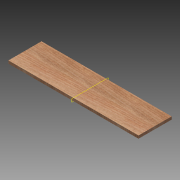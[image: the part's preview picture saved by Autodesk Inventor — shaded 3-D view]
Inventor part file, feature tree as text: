
AUTODESK INVENTOR PART (.ipt)
format: ipt  version: 2015 (Build 190159000, 159)  size: 84,992 bytes
history: native  units: in
note: dims shown in document units (in); Inventor stores cm internally (conversion verified against a paired STEP export)
features: extrude x1, plane x1, sketch x1
ambient origin geometry x8: Origin, YZ Plane, XZ Plane, XY Plane, X Axis, Y Axis, Z Axis, Center Point
bodies: Solid1 (feature_tree)
feature tree (3):
  extrude  "Extrusion1"  Depth=27.5591in
  plane  "Work Plane1"
  sketch  "Sketch1"  dims[d0=7.0079in d1=27.5591in d2=0.5906in d3=0.0in]
